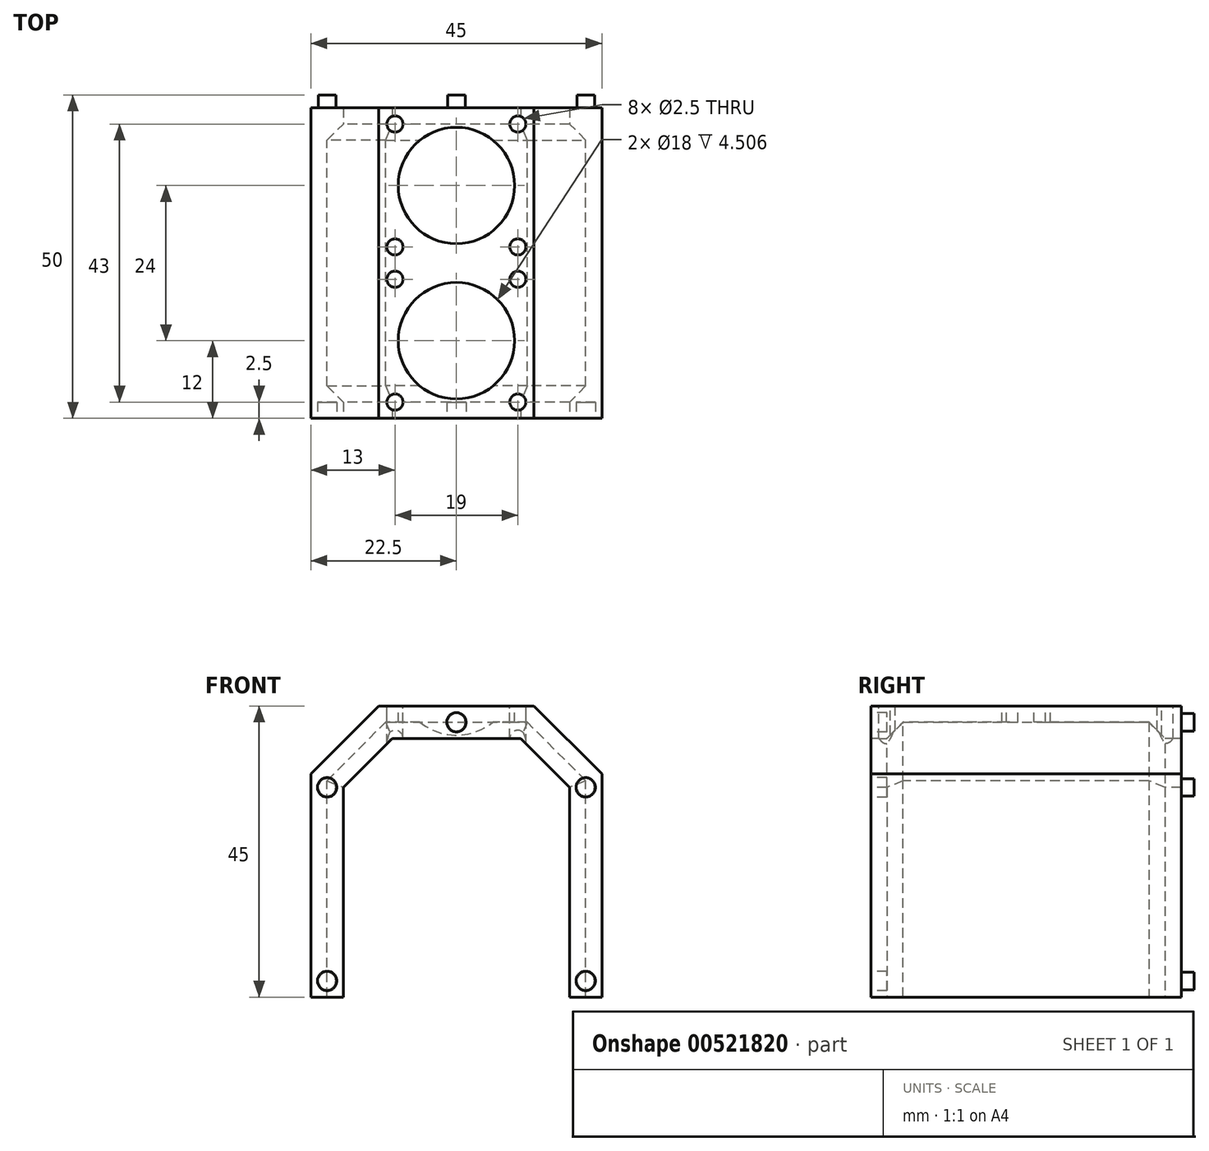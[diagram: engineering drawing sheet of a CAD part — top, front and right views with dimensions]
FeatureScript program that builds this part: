
annotation { "Feature Type Name" : "Feature", "Feature Type Description" : "" }
export const myFeature = defineFeature(function(context is Context, id is Id, definition is map)
    precondition{}
    {
        {
            var Q0;
            Q0=qCreatedBy(makeId("Front.planeOp"),FACE);
            var sketch = newSketch(context, id + "F0", { "sketchPlane" : qUnion([Q0])});
            skLineSegment(sketch, "E0.bottom", {"start": v(22.5, 22.5) * mm, "end": v(-22.5, 22.5) * mm});
            skLineSegment(sketch, "E0.top", {"start": v(22.5, -22.5) * mm, "end": v(-22.5, -22.5) * mm});
            skLineSegment(sketch, "E0.left", {"start": v(22.5, 22.5) * mm, "end": v(22.5, -22.5) * mm});
            skLineSegment(sketch, "E0.right", {"start": v(-22.5, 22.5) * mm, "end": v(-22.5, -22.5) * mm});
            skPoint(sketch, "E0.middle", {"position": v(0, 0) * mm});
            skCircle(sketch, "E1", {"center": v(0, 0) * mm, "radius": 4.25 * mm});
            skSolve(sketch);
        }
        {
            var Q0;
            Q0=makeQuery(id+"F0.imprint","IMPRINT",FACE,{"disambiguationData":[TD([[makeQuery(id+"F0.imprint","IMPRINT",EDGE,{"derivedFrom":sQuery(id+"F0.wireOp",EDGE,"E0.bottom")}),1.0]])]});
            var Q1;
            Q1=makeQuery(id+"F0.imprint","IMPRINT",FACE,{"disambiguationData":[TD([[makeQuery(id+"F0.imprint","IMPRINT",EDGE,{"derivedFrom":sQuery(id+"F0.wireOp",EDGE,"E1")}),1.0]])]});
            extrude(context, id + "F1", {"entities" : qUnion([Q0, Q1]), "depth" : 48 * mm, "offsetDistance" : 25 * mm});
        }
        {
            var Q0;
            Q0=makeQuery(id+"F1.opExtrude","SWEPT_EDGE",EDGE,{"disambiguationData":[OSD([sQuery(id+"F0.wireOp",EDGE,"E0.bottom"),sQuery(id+"F0.wireOp",EDGE,"E0.right")])]});
            var Q1;
            Q1=makeQuery(id+"F1.opExtrude","SWEPT_EDGE",EDGE,{"disambiguationData":[OSD([sQuery(id+"F0.wireOp",EDGE,"E0.bottom"),sQuery(id+"F0.wireOp",EDGE,"E0.left")])]});
            chamfer(context, id + "F2", {"entities" : qUnion([Q0, Q1]), "width" : 10.5 * mm, "tangentPropagation" : true});
        }
        {
            var Q0;
            Q0=makeQuery(id+"F1.opExtrude","SWEPT_FACE",FACE,{"disambiguationData":[OSD([sQuery(id+"F0.wireOp",EDGE,"E0.top")])]});
            shell(context, id + "F3", {"entities" : qUnion([Q0]), "thickness" : 2.5 * mm});
        }
        {
            var Q0;
            Q0=makeQuery(id+"F1.opExtrude","SWEPT_FACE",FACE,{"disambiguationData":[OSD([sQuery(id+"F0.wireOp",EDGE,"E0.bottom")])]});
            var sketch = newSketch(context, id + "F4", { "sketchPlane" : qUnion([Q0])});
            skLineSegment(sketch, "E2", {"start": v(0, -48) * mm, "end": v(0, -36) * mm});
            skPoint(sketch, "E2.endSnap0", {"position": v(0, -48) * mm});
            skLineSegment(sketch, "E3", {"start": v(0, 0) * mm, "end": v(0, -12) * mm});
            skPoint(sketch, "E3.endSnap0", {"position": v(0, 0) * mm});
            skCircle(sketch, "E4", {"center": v(0, -36) * mm, "radius": 9 * mm});
            skCircle(sketch, "E5", {"center": v(0, -12) * mm, "radius": 9 * mm});
            skLineSegment(sketch, "E6.bottom", {"start": v(-12, 0) * mm, "end": v(-9.5, 0) * mm});
            skLineSegment(sketch, "E6.top", {"start": v(-12, -2.5) * mm, "end": v(-9.5, -2.5) * mm});
            skLineSegment(sketch, "E6.left", {"start": v(-12, 0) * mm, "end": v(-12, -2.5) * mm});
            skLineSegment(sketch, "E6.right", {"start": v(-9.5, 0) * mm, "end": v(-9.5, -2.5) * mm});
            skLineSegment(sketch, "E7.bottom", {"start": v(-12, -24) * mm, "end": v(-9.5, -24) * mm});
            skLineSegment(sketch, "E7.top", {"start": v(-12, -21.5) * mm, "end": v(-9.5, -21.5) * mm});
            skLineSegment(sketch, "E7.left", {"start": v(-12, -24) * mm, "end": v(-12, -21.5) * mm});
            skLineSegment(sketch, "E7.right", {"start": v(-9.5, -24) * mm, "end": v(-9.5, -21.5) * mm});
            skLineSegment(sketch, "E8.top", {"start": v(-12, -26.5) * mm, "end": v(-9.5, -26.5) * mm});
            skLineSegment(sketch, "E8.left", {"start": v(-12, -24) * mm, "end": v(-12, -26.5) * mm});
            skLineSegment(sketch, "E8.right", {"start": v(-9.5, -24) * mm, "end": v(-9.5, -26.5) * mm});
            skLineSegment(sketch, "E9.bottom", {"start": v(-12, -48) * mm, "end": v(-9.5, -48) * mm});
            skLineSegment(sketch, "E9.top", {"start": v(-12, -45.5) * mm, "end": v(-9.5, -45.5) * mm});
            skLineSegment(sketch, "E9.left", {"start": v(-12, -48) * mm, "end": v(-12, -45.5) * mm});
            skLineSegment(sketch, "E9.right", {"start": v(-9.5, -48) * mm, "end": v(-9.5, -45.5) * mm});
            skLineSegment(sketch, "E10.bottom", {"start": v(12, -48) * mm, "end": v(9.5, -48) * mm});
            skLineSegment(sketch, "E10.top", {"start": v(12, -45.5) * mm, "end": v(9.5, -45.5) * mm});
            skLineSegment(sketch, "E10.left", {"start": v(12, -48) * mm, "end": v(12, -45.5) * mm});
            skLineSegment(sketch, "E10.right", {"start": v(9.5, -48) * mm, "end": v(9.5, -45.5) * mm});
            skLineSegment(sketch, "E11.bottom", {"start": v(12, 0) * mm, "end": v(9.5, 0) * mm});
            skLineSegment(sketch, "E11.top", {"start": v(12, -2.5) * mm, "end": v(9.5, -2.5) * mm});
            skLineSegment(sketch, "E11.left", {"start": v(12, 0) * mm, "end": v(12, -2.5) * mm});
            skLineSegment(sketch, "E11.right", {"start": v(9.5, 0) * mm, "end": v(9.5, -2.5) * mm});
            skLineSegment(sketch, "E12.bottom", {"start": v(12, -24) * mm, "end": v(9.5, -24) * mm});
            skLineSegment(sketch, "E12.top", {"start": v(12, -21.5) * mm, "end": v(9.5, -21.5) * mm});
            skLineSegment(sketch, "E12.left", {"start": v(12, -24) * mm, "end": v(12, -21.5) * mm});
            skLineSegment(sketch, "E12.right", {"start": v(9.5, -24) * mm, "end": v(9.5, -21.5) * mm});
            skLineSegment(sketch, "E13.top", {"start": v(12, -26.5) * mm, "end": v(9.5, -26.5) * mm});
            skLineSegment(sketch, "E13.left", {"start": v(12, -24) * mm, "end": v(12, -26.5) * mm});
            skLineSegment(sketch, "E13.right", {"start": v(9.5, -24) * mm, "end": v(9.5, -26.5) * mm});
            skCircle(sketch, "E14", {"center": v(-9.5, -45.5) * mm, "radius": 1.25 * mm});
            skCircle(sketch, "E15", {"center": v(-9.5, -26.5) * mm, "radius": 1.25 * mm});
            skCircle(sketch, "E16", {"center": v(-9.5, -21.5) * mm, "radius": 1.25 * mm});
            skCircle(sketch, "E17", {"center": v(-9.5, -2.5) * mm, "radius": 1.25 * mm});
            skCircle(sketch, "E18", {"center": v(9.5, -2.5) * mm, "radius": 1.25 * mm});
            skCircle(sketch, "E19", {"center": v(9.5, -21.5) * mm, "radius": 1.25 * mm});
            skCircle(sketch, "E20", {"center": v(9.5, -26.5) * mm, "radius": 1.25 * mm});
            skCircle(sketch, "E21", {"center": v(9.5, -45.5) * mm, "radius": 1.25 * mm});
            skSolve(sketch);
        }
        {
            var Q0;
            Q0=makeQuery(id+"F4.imprint","IMPRINT",FACE,{"disambiguationData":[TD([[makeQuery(id+"F4.imprint","IMPRINT",EDGE,{"derivedFrom":sQuery(id+"F4.wireOp",EDGE,"E4")}),1.0]])]});
            var Q1;
            Q1=makeQuery(id+"F4.imprint","IMPRINT",FACE,{"disambiguationData":[TD([[makeQuery(id+"F4.imprint","IMPRINT",EDGE,{"derivedFrom":sQuery(id+"F4.wireOp",EDGE,"E5")}),1.0]])]});
            extrude(context, id + "F5", {"entities" : qUnion([Q0, Q1]), "operationType" : NewBodyOperationType.REMOVE, "oppositeDirection" : true, "depth" : 25 * mm, "offsetDistance" : 25 * mm});
        }
        {
            var Q0;
            Q0=makeQuery(id+"F1.opExtrude","CAP_FACE",FACE,{"disambiguationData":[OSD([sQuery(id+"F0.wireOp",EDGE,"E0.bottom"),sQuery(id+"F0.wireOp",EDGE,"E0.top"),sQuery(id+"F0.wireOp",EDGE,"E0.left"),sQuery(id+"F0.wireOp",EDGE,"E0.right")])],"isStart":false});
            var sketch = newSketch(context, id + "F6", { "sketchPlane" : qUnion([Q0])});
            skLineSegment(sketch, "E22.0", {"start": v(-17.5, 9.93) * mm, "end": v(-17.5, -22.5) * mm});
            skLineSegment(sketch, "E22.1", {"start": v(17.5, 9.93) * mm, "end": v(17.5, -22.5) * mm});
            skLineSegment(sketch, "E22.2", {"start": v(17.5, 9.93) * mm, "end": v(9.93, 17.5) * mm});
            skLineSegment(sketch, "E22.3", {"start": v(9.93, 17.5) * mm, "end": v(-9.93, 17.5) * mm});
            skLineSegment(sketch, "E22.4", {"start": v(-9.93, 17.5) * mm, "end": v(-17.5, 9.93) * mm});
            skLineSegment(sketch, "E23.bottom", {"start": v(-22.5, -22.5) * mm, "end": v(-20, -22.5) * mm});
            skLineSegment(sketch, "E23.top", {"start": v(-22.5, -20) * mm, "end": v(-20, -20) * mm});
            skLineSegment(sketch, "E23.left", {"start": v(-22.5, -22.5) * mm, "end": v(-22.5, -20) * mm});
            skLineSegment(sketch, "E23.right", {"start": v(-20, -22.5) * mm, "end": v(-20, -20) * mm});
            skLineSegment(sketch, "E24.bottom", {"start": v(17.5, -22.5) * mm, "end": v(20, -22.5) * mm});
            skLineSegment(sketch, "E24.top", {"start": v(17.5, -20) * mm, "end": v(20, -20) * mm});
            skLineSegment(sketch, "E24.left", {"start": v(17.5, -22.5) * mm, "end": v(17.5, -20) * mm});
            skLineSegment(sketch, "E24.right", {"start": v(20, -22.5) * mm, "end": v(20, -20) * mm});
            skLineSegment(sketch, "E25.bottom", {"start": v(17.5, 9.93) * mm, "end": v(20, 9.93) * mm});
            skLineSegment(sketch, "E25.top", {"start": v(17.5, 7.43) * mm, "end": v(20, 7.43) * mm});
            skLineSegment(sketch, "E25.left", {"start": v(17.5, 9.93) * mm, "end": v(17.5, 7.43) * mm});
            skLineSegment(sketch, "E25.right", {"start": v(20, 9.93) * mm, "end": v(20, 7.43) * mm});
            skLineSegment(sketch, "E26.bottom", {"start": v(-17.5, 9.93) * mm, "end": v(-20, 9.93) * mm});
            skLineSegment(sketch, "E26.top", {"start": v(-17.5, 7.43) * mm, "end": v(-20, 7.43) * mm});
            skLineSegment(sketch, "E26.left", {"start": v(-17.5, 9.93) * mm, "end": v(-17.5, 7.43) * mm});
            skLineSegment(sketch, "E26.right", {"start": v(-20, 9.93) * mm, "end": v(-20, 7.43) * mm});
            skLineSegment(sketch, "E27", {"start": v(0, 17.5) * mm, "end": v(0, 20) * mm});
            skCircle(sketch, "E28", {"center": v(-20, 9.93) * mm, "radius": 1.5 * mm});
            skCircle(sketch, "E29", {"center": v(-20, -20) * mm, "radius": 1.5 * mm});
            skCircle(sketch, "E30", {"center": v(0, 20) * mm, "radius": 1.5 * mm});
            skCircle(sketch, "E31", {"center": v(20, 9.93) * mm, "radius": 1.5 * mm});
            skCircle(sketch, "E32", {"center": v(20, -20) * mm, "radius": 1.5 * mm});
            skSolve(sketch);
        }
        {
            var Q0;
            Q0=makeQuery(id+"F6.imprint","IMPRINT",FACE,{"disambiguationData":[TD([[makeQuery(id+"F6.imprint","IMPRINT",EDGE,{"derivedFrom":sQuery(id+"F6.wireOp",EDGE,"750ff86b-3941-4c00-ad90-e9fef97a6c6d.0")}),1.0]])]});
            var Q1;
            {var subQ1=sQuery(id+"F6.wireOp",EDGE,"E22.0");Q1=makeQuery(id+"F6.imprint","IMPRINT",FACE,{"disambiguationData":[TD([[makeQuery(id+"F6.imprint","IMPRINT",EDGE,{"derivedFrom":subQ1}),1.0]])]});}
            extrude(context, id + "F7", {"entities" : qUnion([Q0, Q1]), "operationType" : NewBodyOperationType.REMOVE, "endBound" : BoundingType.THROUGH_ALL, "oppositeDirection" : true, "depth" : 25 * mm, "offsetDistance" : 25 * mm});
        }
        {
            var Q0;
            Q0=makeQuery(id+"F1.opExtrude","CAP_FACE",FACE,{"disambiguationData":[OSD([sQuery(id+"F0.wireOp",EDGE,"E0.bottom"),sQuery(id+"F0.wireOp",EDGE,"E0.top"),sQuery(id+"F0.wireOp",EDGE,"E0.left"),sQuery(id+"F0.wireOp",EDGE,"E0.right")])],"isStart":true});
            var sketch = newSketch(context, id + "F8", { "sketchPlane" : qUnion([Q0])});
            skLineSegment(sketch, "E33.0", {"start": v(-17.5, 9.93) * mm, "end": v(-17.5, -22.5) * mm});
            skLineSegment(sketch, "E33.1", {"start": v(17.5, 9.93) * mm, "end": v(17.5, -22.5) * mm});
            skLineSegment(sketch, "E33.2", {"start": v(17.5, 9.93) * mm, "end": v(9.93, 17.5) * mm});
            skLineSegment(sketch, "E33.3", {"start": v(9.93, 17.5) * mm, "end": v(-9.93, 17.5) * mm});
            skLineSegment(sketch, "E33.4", {"start": v(-9.93, 17.5) * mm, "end": v(-17.5, 9.93) * mm});
            skLineSegment(sketch, "E34.bottom", {"start": v(-22.5, -22.5) * mm, "end": v(-20, -22.5) * mm});
            skLineSegment(sketch, "E34.top", {"start": v(-22.5, -20) * mm, "end": v(-20, -20) * mm});
            skLineSegment(sketch, "E34.left", {"start": v(-22.5, -22.5) * mm, "end": v(-22.5, -20) * mm});
            skLineSegment(sketch, "E34.right", {"start": v(-20, -22.5) * mm, "end": v(-20, -20) * mm});
            skLineSegment(sketch, "E35.bottom", {"start": v(17.5, -22.5) * mm, "end": v(20, -22.5) * mm});
            skLineSegment(sketch, "E35.top", {"start": v(17.5, -20) * mm, "end": v(20, -20) * mm});
            skLineSegment(sketch, "E35.left", {"start": v(17.5, -22.5) * mm, "end": v(17.5, -20) * mm});
            skLineSegment(sketch, "E35.right", {"start": v(20, -22.5) * mm, "end": v(20, -20) * mm});
            skLineSegment(sketch, "E36.bottom", {"start": v(17.5, 9.93) * mm, "end": v(20, 9.93) * mm});
            skLineSegment(sketch, "E36.top", {"start": v(17.5, 7.43) * mm, "end": v(20, 7.43) * mm});
            skLineSegment(sketch, "E36.left", {"start": v(17.5, 9.93) * mm, "end": v(17.5, 7.43) * mm});
            skLineSegment(sketch, "E36.right", {"start": v(20, 9.93) * mm, "end": v(20, 7.43) * mm});
            skLineSegment(sketch, "E37.bottom", {"start": v(-17.5, 9.93) * mm, "end": v(-20, 9.93) * mm});
            skLineSegment(sketch, "E37.top", {"start": v(-17.5, 7.43) * mm, "end": v(-20, 7.43) * mm});
            skLineSegment(sketch, "E37.left", {"start": v(-17.5, 9.93) * mm, "end": v(-17.5, 7.43) * mm});
            skLineSegment(sketch, "E37.right", {"start": v(-20, 9.93) * mm, "end": v(-20, 7.43) * mm});
            skLineSegment(sketch, "E38", {"start": v(0, 17.5) * mm, "end": v(0, 20) * mm});
            skCircle(sketch, "E39", {"center": v(-20, 9.93) * mm, "radius": 1.35 * mm});
            skCircle(sketch, "E40", {"center": v(-20, -20) * mm, "radius": 1.35 * mm});
            skCircle(sketch, "E41", {"center": v(0, 20) * mm, "radius": 1.35 * mm});
            skCircle(sketch, "E42", {"center": v(20, 9.93) * mm, "radius": 1.35 * mm});
            skCircle(sketch, "E43", {"center": v(20, -20) * mm, "radius": 1.35 * mm});
            skSolve(sketch);
        }
        {
            var Q0;
            {var subQ0=sQuery(id+"F8.wireOp",EDGE,"E35.right");var subQ1=sQuery(id+"F8.wireOp",EDGE,"E35.top");var subQ2=makeQuery(id+"F8.imprint","INTERSECT",VERTEX,{"derivedFrom":[subQ1,subQ0]});Q0=makeQuery(id+"F8.imprint","IMPRINT",FACE,{"disambiguationData":[TD([[makeQuery(id+"F8.imprint","IMPRINT",EDGE,{"disambiguationData":[TD([[subQ2,1.0]])],"derivedFrom":subQ1}),1.0]])]});}
            var Q1;
            {var subQ0=sQuery(id+"F8.wireOp",EDGE,"E35.right");var subQ1=sQuery(id+"F8.wireOp",EDGE,"E35.top");var subQ2=makeQuery(id+"F8.imprint","INTERSECT",VERTEX,{"derivedFrom":[subQ1,subQ0]});Q1=makeQuery(id+"F8.imprint","IMPRINT",FACE,{"disambiguationData":[TD([[makeQuery(id+"F8.imprint","IMPRINT",EDGE,{"disambiguationData":[TD([[subQ2,1.0]])],"derivedFrom":subQ1}),-1.0]])]});}
            var Q2;
            {var subQ0=sQuery(id+"F8.wireOp",EDGE,"E34.right");var subQ1=sQuery(id+"F8.wireOp",EDGE,"E34.top");var subQ2=makeQuery(id+"F8.imprint","INTERSECT",VERTEX,{"derivedFrom":[subQ1,subQ0]});Q2=makeQuery(id+"F8.imprint","IMPRINT",FACE,{"disambiguationData":[TD([[makeQuery(id+"F8.imprint","IMPRINT",EDGE,{"disambiguationData":[TD([[subQ2,1.0]])],"derivedFrom":subQ1}),1.0]])]});}
            var Q3;
            {var subQ0=sQuery(id+"F8.wireOp",EDGE,"E34.right");var subQ1=sQuery(id+"F8.wireOp",EDGE,"E34.top");var subQ2=makeQuery(id+"F8.imprint","INTERSECT",VERTEX,{"derivedFrom":[subQ1,subQ0]});Q3=makeQuery(id+"F8.imprint","IMPRINT",FACE,{"disambiguationData":[TD([[makeQuery(id+"F8.imprint","IMPRINT",EDGE,{"disambiguationData":[TD([[subQ2,1.0]])],"derivedFrom":subQ1}),-1.0]])]});}
            var Q4;
            {var subQ0=sQuery(id+"F8.wireOp",EDGE,"E37.right");var subQ1=sQuery(id+"F8.wireOp",EDGE,"E37.bottom");var subQ2=makeQuery(id+"F8.imprint","INTERSECT",VERTEX,{"derivedFrom":[subQ1,subQ0]});Q4=makeQuery(id+"F8.imprint","IMPRINT",FACE,{"disambiguationData":[TD([[makeQuery(id+"F8.imprint","IMPRINT",EDGE,{"disambiguationData":[TD([[subQ2,1.0]])],"derivedFrom":subQ1}),1.0]])]});}
            var Q5;
            {var subQ0=sQuery(id+"F8.wireOp",EDGE,"E37.right");var subQ1=sQuery(id+"F8.wireOp",EDGE,"E37.bottom");var subQ2=makeQuery(id+"F8.imprint","INTERSECT",VERTEX,{"derivedFrom":[subQ1,subQ0]});Q5=makeQuery(id+"F8.imprint","IMPRINT",FACE,{"disambiguationData":[TD([[makeQuery(id+"F8.imprint","IMPRINT",EDGE,{"disambiguationData":[TD([[subQ2,1.0]])],"derivedFrom":subQ1}),-1.0]])]});}
            var Q6;
            Q6=makeQuery(id+"F8.imprint","IMPRINT",FACE,{"disambiguationData":[TD([[makeQuery(id+"F8.imprint","IMPRINT",EDGE,{"derivedFrom":sQuery(id+"F8.wireOp",EDGE,"E41")}),1.0]])]});
            var Q7;
            {var subQ0=sQuery(id+"F8.wireOp",EDGE,"E36.right");var subQ1=sQuery(id+"F8.wireOp",EDGE,"E36.bottom");var subQ2=makeQuery(id+"F8.imprint","INTERSECT",VERTEX,{"derivedFrom":[subQ1,subQ0]});Q7=makeQuery(id+"F8.imprint","IMPRINT",FACE,{"disambiguationData":[TD([[makeQuery(id+"F8.imprint","IMPRINT",EDGE,{"disambiguationData":[TD([[subQ2,1.0]])],"derivedFrom":subQ1}),1.0]])]});}
            var Q8;
            {var subQ0=sQuery(id+"F8.wireOp",EDGE,"E36.right");var subQ1=sQuery(id+"F8.wireOp",EDGE,"E36.bottom");var subQ2=makeQuery(id+"F8.imprint","INTERSECT",VERTEX,{"derivedFrom":[subQ1,subQ0]});Q8=makeQuery(id+"F8.imprint","IMPRINT",FACE,{"disambiguationData":[TD([[makeQuery(id+"F8.imprint","IMPRINT",EDGE,{"disambiguationData":[TD([[subQ2,1.0]])],"derivedFrom":subQ1}),-1.0]])]});}
            extrude(context, id + "F9", {"entities" : qUnion([Q0, Q1, Q2, Q3, Q4, Q5, Q6, Q7, Q8]), "operationType" : NewBodyOperationType.ADD, "depth" : 2 * mm, "offsetDistance" : 25 * mm});
        }
        {
            var Q0;
            {var subQ0=sQuery(id+"F0.wireOp",EDGE,"E0.left");Q0=makeQuery(id+"F3.opShell","OFFSET_EDGE",EDGE,{"disambiguationData":[OSD([subQ0]),TDD([makeQuery(id+"F1.opExtrude","CAP_EDGE",EDGE,{"disambiguationData":[OSD([subQ0])],"isStart":false})])]});}
            var Q1;
            {var subQ0=sQuery(id+"F0.wireOp",EDGE,"E0.right");var subQ1=sQuery(id+"F0.wireOp",EDGE,"E0.left");var subQ2=sQuery(id+"F0.wireOp",EDGE,"E0.top");var subQ3=sQuery(id+"F0.wireOp",EDGE,"E0.bottom");Q1=makeQuery(id+"F3.opShell","OFFSET_EDGE",EDGE,{"disambiguationData":[OSD([subQ3,subQ2,subQ1,subQ0]),TDD([makeQuery(id+"F2.opChamfer","BLEND_EDGE",EDGE,{"blendedFrom":[makeQuery(id+"F1.opExtrude","SWEPT_EDGE",EDGE,{"disambiguationData":[OSD([subQ3,subQ1])]}),makeQuery(id+"F1.opExtrude","CAP_FACE",FACE,{"disambiguationData":[OSD([subQ3,subQ2,subQ1,subQ0])],"isStart":false})],"blendedInto":[makeQuery(id+"F1.opExtrude","CAP_FACE",FACE,{"disambiguationData":[OSD([subQ3,subQ2,subQ1,subQ0])],"isStart":false})]})])]});}
            var Q2;
            {var subQ0=sQuery(id+"F0.wireOp",EDGE,"E0.bottom");Q2=makeQuery(id+"F3.opShell","OFFSET_EDGE",EDGE,{"disambiguationData":[OSD([subQ0]),TDD([makeQuery(id+"F1.opExtrude","CAP_EDGE",EDGE,{"disambiguationData":[OSD([subQ0])],"isStart":false})])]});}
            var Q3;
            {var subQ0=sQuery(id+"F0.wireOp",EDGE,"E0.right");var subQ1=sQuery(id+"F0.wireOp",EDGE,"E0.left");var subQ2=sQuery(id+"F0.wireOp",EDGE,"E0.top");var subQ3=sQuery(id+"F0.wireOp",EDGE,"E0.bottom");Q3=makeQuery(id+"F3.opShell","OFFSET_EDGE",EDGE,{"disambiguationData":[OSD([subQ3,subQ2,subQ1,subQ0]),TDD([makeQuery(id+"F2.opChamfer","BLEND_EDGE",EDGE,{"blendedFrom":[makeQuery(id+"F1.opExtrude","SWEPT_EDGE",EDGE,{"disambiguationData":[OSD([subQ3,subQ0])]}),makeQuery(id+"F1.opExtrude","CAP_FACE",FACE,{"disambiguationData":[OSD([subQ3,subQ2,subQ1,subQ0])],"isStart":false})],"blendedInto":[makeQuery(id+"F1.opExtrude","CAP_FACE",FACE,{"disambiguationData":[OSD([subQ3,subQ2,subQ1,subQ0])],"isStart":false})]})])]});}
            var Q4;
            {var subQ0=sQuery(id+"F0.wireOp",EDGE,"E0.right");Q4=makeQuery(id+"F3.opShell","OFFSET_EDGE",EDGE,{"disambiguationData":[OSD([subQ0]),TDD([makeQuery(id+"F1.opExtrude","CAP_EDGE",EDGE,{"disambiguationData":[OSD([subQ0])],"isStart":false})])]});}
            var Q5;
            {var subQ0=sQuery(id+"F0.wireOp",EDGE,"E0.right");Q5=makeQuery(id+"F3.opShell","OFFSET_EDGE",EDGE,{"disambiguationData":[OSD([subQ0]),TDD([makeQuery(id+"F1.opExtrude","CAP_EDGE",EDGE,{"disambiguationData":[OSD([subQ0])],"isStart":true})])]});}
            var Q6;
            {var subQ0=sQuery(id+"F0.wireOp",EDGE,"E0.right");var subQ1=sQuery(id+"F0.wireOp",EDGE,"E0.left");var subQ2=sQuery(id+"F0.wireOp",EDGE,"E0.top");var subQ3=sQuery(id+"F0.wireOp",EDGE,"E0.bottom");Q6=makeQuery(id+"F3.opShell","OFFSET_EDGE",EDGE,{"disambiguationData":[OSD([subQ3,subQ2,subQ1,subQ0]),TDD([makeQuery(id+"F2.opChamfer","BLEND_EDGE",EDGE,{"blendedFrom":[makeQuery(id+"F1.opExtrude","SWEPT_EDGE",EDGE,{"disambiguationData":[OSD([subQ3,subQ0])]}),makeQuery(id+"F1.opExtrude","CAP_FACE",FACE,{"disambiguationData":[OSD([subQ3,subQ2,subQ1,subQ0])],"isStart":true})],"blendedInto":[makeQuery(id+"F1.opExtrude","CAP_FACE",FACE,{"disambiguationData":[OSD([subQ3,subQ2,subQ1,subQ0])],"isStart":true})]})])]});}
            var Q7;
            {var subQ0=sQuery(id+"F0.wireOp",EDGE,"E0.bottom");Q7=makeQuery(id+"F3.opShell","OFFSET_EDGE",EDGE,{"disambiguationData":[OSD([subQ0]),TDD([makeQuery(id+"F1.opExtrude","CAP_EDGE",EDGE,{"disambiguationData":[OSD([subQ0])],"isStart":true})])]});}
            var Q8;
            {var subQ0=sQuery(id+"F0.wireOp",EDGE,"E0.right");var subQ1=sQuery(id+"F0.wireOp",EDGE,"E0.left");var subQ2=sQuery(id+"F0.wireOp",EDGE,"E0.top");var subQ3=sQuery(id+"F0.wireOp",EDGE,"E0.bottom");Q8=makeQuery(id+"F3.opShell","OFFSET_EDGE",EDGE,{"disambiguationData":[OSD([subQ3,subQ2,subQ1,subQ0]),TDD([makeQuery(id+"F2.opChamfer","BLEND_EDGE",EDGE,{"blendedFrom":[makeQuery(id+"F1.opExtrude","SWEPT_EDGE",EDGE,{"disambiguationData":[OSD([subQ3,subQ1])]}),makeQuery(id+"F1.opExtrude","CAP_FACE",FACE,{"disambiguationData":[OSD([subQ3,subQ2,subQ1,subQ0])],"isStart":true})],"blendedInto":[makeQuery(id+"F1.opExtrude","CAP_FACE",FACE,{"disambiguationData":[OSD([subQ3,subQ2,subQ1,subQ0])],"isStart":true})]})])]});}
            var Q9;
            {var subQ0=sQuery(id+"F0.wireOp",EDGE,"E0.left");Q9=makeQuery(id+"F3.opShell","OFFSET_EDGE",EDGE,{"disambiguationData":[OSD([subQ0]),TDD([makeQuery(id+"F1.opExtrude","CAP_EDGE",EDGE,{"disambiguationData":[OSD([subQ0])],"isStart":true})])]});}
            chamfer(context, id + "F10", {"entities" : qUnion([Q0, Q1, Q2, Q3, Q4, Q5, Q6, Q7, Q8, Q9]), "width" : 2.5 * mm, "tangentPropagation" : true});
        }
        {
            var Q0;
            Q0=makeQuery(id+"F6.imprint","IMPRINT",FACE,{"disambiguationData":[TD([[makeQuery(id+"F6.imprint","IMPRINT",EDGE,{"derivedFrom":sQuery(id+"F6.wireOp",EDGE,"E30")}),1.0]])]});
            var Q1;
            {var subQ0=sQuery(id+"F6.wireOp",EDGE,"E25.right");var subQ1=sQuery(id+"F6.wireOp",EDGE,"E25.bottom");var subQ2=makeQuery(id+"F6.imprint","INTERSECT",VERTEX,{"derivedFrom":[subQ1,subQ0]});Q1=makeQuery(id+"F6.imprint","IMPRINT",FACE,{"disambiguationData":[TD([[makeQuery(id+"F6.imprint","IMPRINT",EDGE,{"disambiguationData":[TD([[subQ2,1.0]])],"derivedFrom":subQ1}),1.0]])]});}
            var Q2;
            {var subQ0=sQuery(id+"F6.wireOp",EDGE,"E25.right");var subQ1=sQuery(id+"F6.wireOp",EDGE,"E25.bottom");var subQ2=makeQuery(id+"F6.imprint","INTERSECT",VERTEX,{"derivedFrom":[subQ1,subQ0]});Q2=makeQuery(id+"F6.imprint","IMPRINT",FACE,{"disambiguationData":[TD([[makeQuery(id+"F6.imprint","IMPRINT",EDGE,{"disambiguationData":[TD([[subQ2,1.0]])],"derivedFrom":subQ1}),-1.0]])]});}
            var Q3;
            {var subQ0=sQuery(id+"F6.wireOp",EDGE,"E24.right");var subQ1=sQuery(id+"F6.wireOp",EDGE,"E24.top");var subQ2=makeQuery(id+"F6.imprint","INTERSECT",VERTEX,{"derivedFrom":[subQ1,subQ0]});Q3=makeQuery(id+"F6.imprint","IMPRINT",FACE,{"disambiguationData":[TD([[makeQuery(id+"F6.imprint","IMPRINT",EDGE,{"disambiguationData":[TD([[subQ2,1.0]])],"derivedFrom":subQ1}),1.0]])]});}
            var Q4;
            {var subQ0=sQuery(id+"F6.wireOp",EDGE,"E24.right");var subQ1=sQuery(id+"F6.wireOp",EDGE,"E24.top");var subQ2=makeQuery(id+"F6.imprint","INTERSECT",VERTEX,{"derivedFrom":[subQ1,subQ0]});Q4=makeQuery(id+"F6.imprint","IMPRINT",FACE,{"disambiguationData":[TD([[makeQuery(id+"F6.imprint","IMPRINT",EDGE,{"disambiguationData":[TD([[subQ2,1.0]])],"derivedFrom":subQ1}),-1.0]])]});}
            var Q5;
            {var subQ0=sQuery(id+"F6.wireOp",EDGE,"E23.right");var subQ1=sQuery(id+"F6.wireOp",EDGE,"E23.top");var subQ2=makeQuery(id+"F6.imprint","INTERSECT",VERTEX,{"derivedFrom":[subQ1,subQ0]});Q5=makeQuery(id+"F6.imprint","IMPRINT",FACE,{"disambiguationData":[TD([[makeQuery(id+"F6.imprint","IMPRINT",EDGE,{"disambiguationData":[TD([[subQ2,1.0]])],"derivedFrom":subQ1}),1.0]])]});}
            var Q6;
            {var subQ0=sQuery(id+"F6.wireOp",EDGE,"E23.right");var subQ1=sQuery(id+"F6.wireOp",EDGE,"E23.top");var subQ2=makeQuery(id+"F6.imprint","INTERSECT",VERTEX,{"derivedFrom":[subQ1,subQ0]});Q6=makeQuery(id+"F6.imprint","IMPRINT",FACE,{"disambiguationData":[TD([[makeQuery(id+"F6.imprint","IMPRINT",EDGE,{"disambiguationData":[TD([[subQ2,1.0]])],"derivedFrom":subQ1}),-1.0]])]});}
            var Q7;
            {var subQ0=sQuery(id+"F6.wireOp",EDGE,"E26.right");var subQ1=sQuery(id+"F6.wireOp",EDGE,"E26.bottom");var subQ2=makeQuery(id+"F6.imprint","INTERSECT",VERTEX,{"derivedFrom":[subQ1,subQ0]});Q7=makeQuery(id+"F6.imprint","IMPRINT",FACE,{"disambiguationData":[TD([[makeQuery(id+"F6.imprint","IMPRINT",EDGE,{"disambiguationData":[TD([[subQ2,1.0]])],"derivedFrom":subQ1}),1.0]])]});}
            var Q8;
            {var subQ0=sQuery(id+"F6.wireOp",EDGE,"E26.right");var subQ1=sQuery(id+"F6.wireOp",EDGE,"E26.bottom");var subQ2=makeQuery(id+"F6.imprint","INTERSECT",VERTEX,{"derivedFrom":[subQ1,subQ0]});Q8=makeQuery(id+"F6.imprint","IMPRINT",FACE,{"disambiguationData":[TD([[makeQuery(id+"F6.imprint","IMPRINT",EDGE,{"disambiguationData":[TD([[subQ2,1.0]])],"derivedFrom":subQ1}),-1.0]])]});}
            extrude(context, id + "F11", {"entities" : qUnion([Q0, Q1, Q2, Q3, Q4, Q5, Q6, Q7, Q8]), "operationType" : NewBodyOperationType.REMOVE, "oppositeDirection" : true, "depth" : 2.5 * mm, "offsetDistance" : 25 * mm});
        }
        {
            var Q0;
            {var subQ0=sQuery(id+"F4.wireOp",EDGE,"E10.right");var subQ1=sQuery(id+"F4.wireOp",EDGE,"E10.top");var subQ2=makeQuery(id+"F4.imprint","INTERSECT",VERTEX,{"derivedFrom":[subQ1,subQ0]});Q0=makeQuery(id+"F4.imprint","IMPRINT",FACE,{"disambiguationData":[TD([[makeQuery(id+"F4.imprint","IMPRINT",EDGE,{"disambiguationData":[TD([[subQ2,1.0]])],"derivedFrom":subQ1}),-1.0]])]});}
            var Q1;
            {var subQ0=sQuery(id+"F4.wireOp",EDGE,"E10.right");var subQ1=sQuery(id+"F4.wireOp",EDGE,"E10.top");var subQ2=makeQuery(id+"F4.imprint","INTERSECT",VERTEX,{"derivedFrom":[subQ1,subQ0]});Q1=makeQuery(id+"F4.imprint","IMPRINT",FACE,{"disambiguationData":[TD([[makeQuery(id+"F4.imprint","IMPRINT",EDGE,{"disambiguationData":[TD([[subQ2,1.0]])],"derivedFrom":subQ1}),1.0]])]});}
            var Q2;
            {var subQ0=sQuery(id+"F4.wireOp",EDGE,"E13.right");var subQ1=sQuery(id+"F4.wireOp",EDGE,"E13.top");var subQ2=makeQuery(id+"F4.imprint","INTERSECT",VERTEX,{"derivedFrom":[subQ1,subQ0]});Q2=makeQuery(id+"F4.imprint","IMPRINT",FACE,{"disambiguationData":[TD([[makeQuery(id+"F4.imprint","IMPRINT",EDGE,{"disambiguationData":[TD([[subQ2,1.0]])],"derivedFrom":subQ1}),1.0]])]});}
            var Q3;
            {var subQ0=sQuery(id+"F4.wireOp",EDGE,"E13.right");var subQ1=sQuery(id+"F4.wireOp",EDGE,"E13.top");var subQ2=makeQuery(id+"F4.imprint","INTERSECT",VERTEX,{"derivedFrom":[subQ1,subQ0]});Q3=makeQuery(id+"F4.imprint","IMPRINT",FACE,{"disambiguationData":[TD([[makeQuery(id+"F4.imprint","IMPRINT",EDGE,{"disambiguationData":[TD([[subQ2,1.0]])],"derivedFrom":subQ1}),-1.0]])]});}
            var Q4;
            {var subQ0=sQuery(id+"F4.wireOp",EDGE,"E12.right");var subQ1=sQuery(id+"F4.wireOp",EDGE,"E12.top");var subQ2=makeQuery(id+"F4.imprint","INTERSECT",VERTEX,{"derivedFrom":[subQ1,subQ0]});Q4=makeQuery(id+"F4.imprint","IMPRINT",FACE,{"disambiguationData":[TD([[makeQuery(id+"F4.imprint","IMPRINT",EDGE,{"disambiguationData":[TD([[subQ2,1.0]])],"derivedFrom":subQ1}),1.0]])]});}
            var Q5;
            {var subQ0=sQuery(id+"F4.wireOp",EDGE,"E12.right");var subQ1=sQuery(id+"F4.wireOp",EDGE,"E12.top");var subQ2=makeQuery(id+"F4.imprint","INTERSECT",VERTEX,{"derivedFrom":[subQ1,subQ0]});Q5=makeQuery(id+"F4.imprint","IMPRINT",FACE,{"disambiguationData":[TD([[makeQuery(id+"F4.imprint","IMPRINT",EDGE,{"disambiguationData":[TD([[subQ2,1.0]])],"derivedFrom":subQ1}),-1.0]])]});}
            var Q6;
            {var subQ0=sQuery(id+"F4.wireOp",EDGE,"E11.right");var subQ1=sQuery(id+"F4.wireOp",EDGE,"E11.top");var subQ2=makeQuery(id+"F4.imprint","INTERSECT",VERTEX,{"derivedFrom":[subQ1,subQ0]});Q6=makeQuery(id+"F4.imprint","IMPRINT",FACE,{"disambiguationData":[TD([[makeQuery(id+"F4.imprint","IMPRINT",EDGE,{"disambiguationData":[TD([[subQ2,1.0]])],"derivedFrom":subQ1}),1.0]])]});}
            var Q7;
            {var subQ0=sQuery(id+"F4.wireOp",EDGE,"E11.right");var subQ1=sQuery(id+"F4.wireOp",EDGE,"E11.top");var subQ2=makeQuery(id+"F4.imprint","INTERSECT",VERTEX,{"derivedFrom":[subQ1,subQ0]});Q7=makeQuery(id+"F4.imprint","IMPRINT",FACE,{"disambiguationData":[TD([[makeQuery(id+"F4.imprint","IMPRINT",EDGE,{"disambiguationData":[TD([[subQ2,1.0]])],"derivedFrom":subQ1}),-1.0]])]});}
            var Q8;
            {var subQ0=sQuery(id+"F4.wireOp",EDGE,"E6.right");var subQ1=sQuery(id+"F4.wireOp",EDGE,"E6.top");var subQ2=makeQuery(id+"F4.imprint","INTERSECT",VERTEX,{"derivedFrom":[subQ1,subQ0]});Q8=makeQuery(id+"F4.imprint","IMPRINT",FACE,{"disambiguationData":[TD([[makeQuery(id+"F4.imprint","IMPRINT",EDGE,{"disambiguationData":[TD([[subQ2,1.0]])],"derivedFrom":subQ1}),-1.0]])]});}
            var Q9;
            {var subQ0=sQuery(id+"F4.wireOp",EDGE,"E6.right");var subQ1=sQuery(id+"F4.wireOp",EDGE,"E6.top");var subQ2=makeQuery(id+"F4.imprint","INTERSECT",VERTEX,{"derivedFrom":[subQ1,subQ0]});Q9=makeQuery(id+"F4.imprint","IMPRINT",FACE,{"disambiguationData":[TD([[makeQuery(id+"F4.imprint","IMPRINT",EDGE,{"disambiguationData":[TD([[subQ2,1.0]])],"derivedFrom":subQ1}),1.0]])]});}
            var Q10;
            {var subQ0=sQuery(id+"F4.wireOp",EDGE,"E7.right");var subQ1=sQuery(id+"F4.wireOp",EDGE,"E7.top");var subQ2=makeQuery(id+"F4.imprint","INTERSECT",VERTEX,{"derivedFrom":[subQ1,subQ0]});Q10=makeQuery(id+"F4.imprint","IMPRINT",FACE,{"disambiguationData":[TD([[makeQuery(id+"F4.imprint","IMPRINT",EDGE,{"disambiguationData":[TD([[subQ2,1.0]])],"derivedFrom":subQ1}),1.0]])]});}
            var Q11;
            {var subQ0=sQuery(id+"F4.wireOp",EDGE,"E7.right");var subQ1=sQuery(id+"F4.wireOp",EDGE,"E7.top");var subQ2=makeQuery(id+"F4.imprint","INTERSECT",VERTEX,{"derivedFrom":[subQ1,subQ0]});Q11=makeQuery(id+"F4.imprint","IMPRINT",FACE,{"disambiguationData":[TD([[makeQuery(id+"F4.imprint","IMPRINT",EDGE,{"disambiguationData":[TD([[subQ2,1.0]])],"derivedFrom":subQ1}),-1.0]])]});}
            var Q12;
            {var subQ0=sQuery(id+"F4.wireOp",EDGE,"E8.right");var subQ1=sQuery(id+"F4.wireOp",EDGE,"E8.top");var subQ2=makeQuery(id+"F4.imprint","INTERSECT",VERTEX,{"derivedFrom":[subQ1,subQ0]});Q12=makeQuery(id+"F4.imprint","IMPRINT",FACE,{"disambiguationData":[TD([[makeQuery(id+"F4.imprint","IMPRINT",EDGE,{"disambiguationData":[TD([[subQ2,1.0]])],"derivedFrom":subQ1}),1.0]])]});}
            var Q13;
            {var subQ0=sQuery(id+"F4.wireOp",EDGE,"E8.right");var subQ1=sQuery(id+"F4.wireOp",EDGE,"E8.top");var subQ2=makeQuery(id+"F4.imprint","INTERSECT",VERTEX,{"derivedFrom":[subQ1,subQ0]});Q13=makeQuery(id+"F4.imprint","IMPRINT",FACE,{"disambiguationData":[TD([[makeQuery(id+"F4.imprint","IMPRINT",EDGE,{"disambiguationData":[TD([[subQ2,1.0]])],"derivedFrom":subQ1}),-1.0]])]});}
            var Q14;
            {var subQ0=sQuery(id+"F4.wireOp",EDGE,"E9.right");var subQ1=sQuery(id+"F4.wireOp",EDGE,"E9.top");var subQ2=makeQuery(id+"F4.imprint","INTERSECT",VERTEX,{"derivedFrom":[subQ1,subQ0]});Q14=makeQuery(id+"F4.imprint","IMPRINT",FACE,{"disambiguationData":[TD([[makeQuery(id+"F4.imprint","IMPRINT",EDGE,{"disambiguationData":[TD([[subQ2,1.0]])],"derivedFrom":subQ1}),1.0]])]});}
            var Q15;
            {var subQ0=sQuery(id+"F4.wireOp",EDGE,"E9.right");var subQ1=sQuery(id+"F4.wireOp",EDGE,"E9.top");var subQ2=makeQuery(id+"F4.imprint","INTERSECT",VERTEX,{"derivedFrom":[subQ1,subQ0]});Q15=makeQuery(id+"F4.imprint","IMPRINT",FACE,{"disambiguationData":[TD([[makeQuery(id+"F4.imprint","IMPRINT",EDGE,{"disambiguationData":[TD([[subQ2,1.0]])],"derivedFrom":subQ1}),-1.0]])]});}
            extrude(context, id + "F12", {"entities" : qUnion([Q0, Q1, Q2, Q3, Q4, Q5, Q6, Q7, Q8, Q9, Q10, Q11, Q12, Q13, Q14, Q15]), "operationType" : NewBodyOperationType.REMOVE, "oppositeDirection" : true, "depth" : 25 * mm, "offsetDistance" : 25 * mm});
        }
    });
